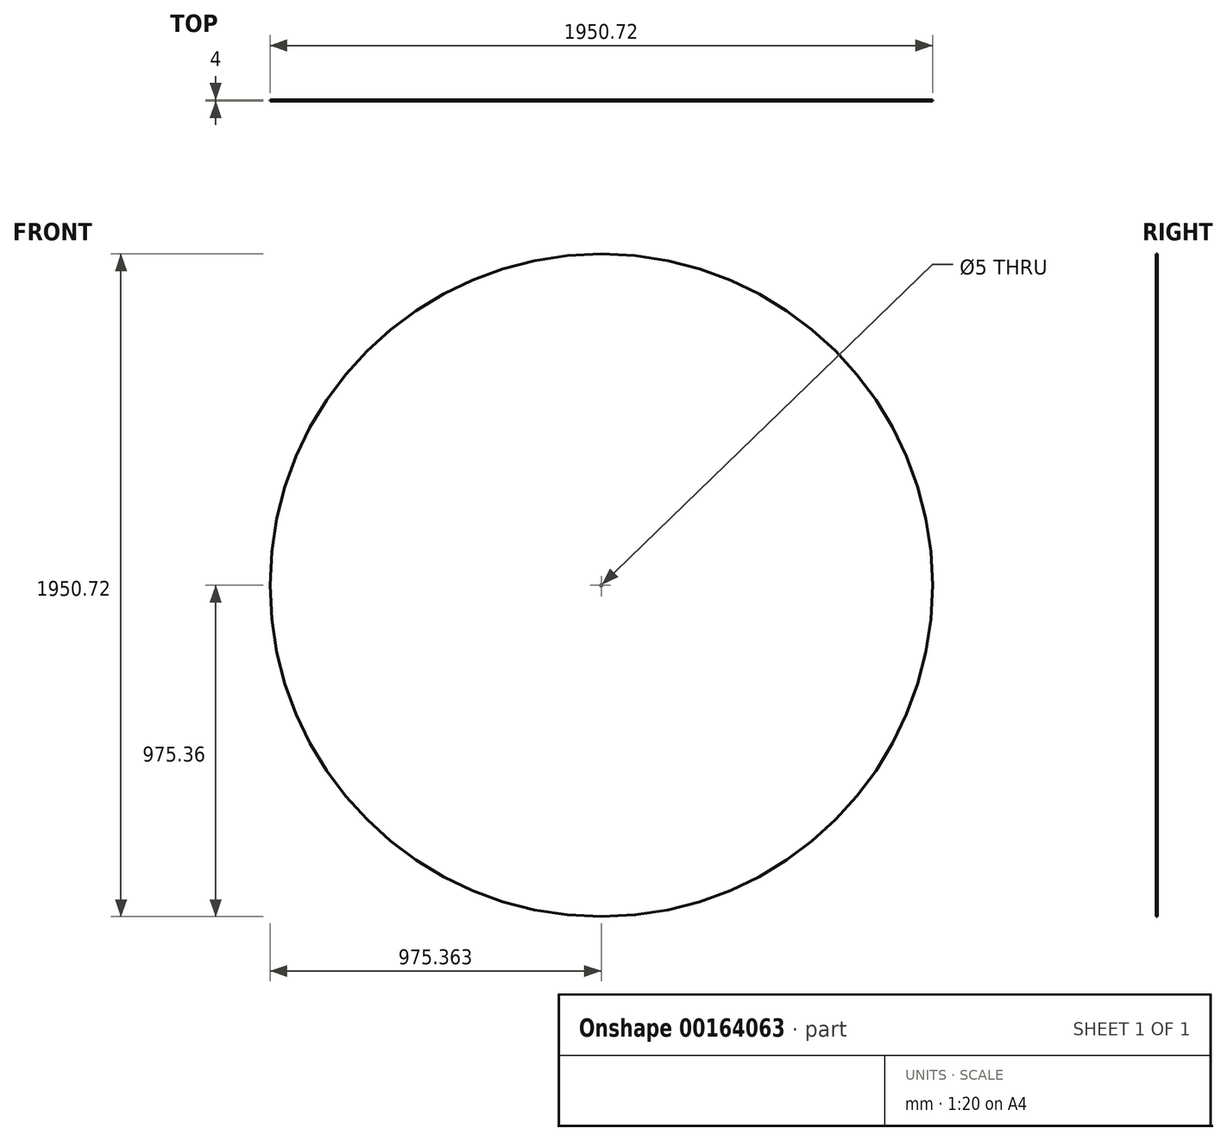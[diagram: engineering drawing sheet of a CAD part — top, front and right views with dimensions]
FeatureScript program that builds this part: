
annotation { "Feature Type Name" : "Feature", "Feature Type Description" : "" }
export const myFeature = defineFeature(function(context is Context, id is Id, definition is map)
    precondition{}
    {
        {
            var Q0;
            Q0=qCreatedBy(makeId("Front.planeOp"),FACE);
            var sketch = newSketch(context, id + "F0", { "sketchPlane" : qUnion([Q0])});
            skCircle(sketch, "E0", {"center": v(-21.68, -26.67) * mm, "radius": 152.4 * mm});
            skCircle(sketch, "E1", {"center": v(-21.68, -26.67) * mm, "radius": 975.36 * mm});
            skSolve(sketch);
        }
        {
            var Q0;
            Q0=makeQuery(id+"F0.imprint","IMPRINT",FACE,{"disambiguationData":[TD([[makeQuery(id+"F0.imprint","IMPRINT",EDGE,{"derivedFrom":sQuery(id+"F0.wireOp",EDGE,"E0")}),1.0]])]});
            var Q1;
            Q1=makeQuery(id+"F0.imprint","IMPRINT",FACE,{"disambiguationData":[TD([[makeQuery(id+"F0.imprint","IMPRINT",EDGE,{"derivedFrom":sQuery(id+"F0.wireOp",EDGE,"E0")}),-1.0]])]});
            extrude(context, id + "F1", {"entities" : qUnion([Q0, Q1]), "depth" : 4 * mm});
        }
        {
            var Q0;
            Q0=sQuery(id+"F0.wireOp",VERTEX,"E0.center");
            var Q1;
            Q1=makeQuery(id+"F1.opExtrude","SWEPT_BODY",BODY,{"disambiguationData":[OSD([sQuery(id+"F0.wireOp",EDGE,"E1")])]});
            hole(context, id + "F2", {"style" : HoleStyle.SIMPLE, "endStyle" : HoleEndStyle.THROUGH, "oppositeDirection" : true, "holeDiameter" : 5 * mm, "locations" : qUnion([Q0]), "scope" : qUnion([Q1]), "isTappedThrough" : true});
        }
    });
